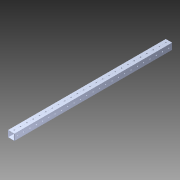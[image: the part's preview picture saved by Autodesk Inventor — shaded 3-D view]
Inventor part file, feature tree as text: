
AUTODESK INVENTOR PART (.ipt)
format: ipt  version: 2014 SP1 (Build 180222100, 222)  size: 1,228,800 bytes
history: native  units: in
note: dims shown in document units (in); Inventor stores cm internally (conversion verified against a paired STEP export)
features: pattern_circular x1, other x1, extrude x1, imported_body x1, sketch x1
ambient origin geometry x8: Origin, YZ Plane, XZ Plane, XY Plane, X Axis, Y Axis, Z Axis, Center Point
bodies: Body1 (feature_tree)
feature tree (5):
  pattern_circular  "CirPattern2"
  other  "1x1 tube1"
  extrude  "Extrusion1"  [1 undecoded]
  imported_body  "Base1"
  sketch  "Sketch1"  dims[d0=34.0in d1=0.0in]
note: 1 required parameter value undecoded (feature->parameter linkage not recoverable at this tier; creation-order binding heuristic only, values carry confidence <= 0.55)
